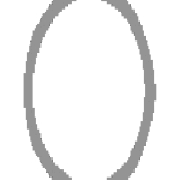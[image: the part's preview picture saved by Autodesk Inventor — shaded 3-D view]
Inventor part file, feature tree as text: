
AUTODESK INVENTOR PART (.ipt)
format: ipt  version: 2021 (Build 250183000, 183)  size: 112,640 bytes
history: native  units: in
note: dims shown in document units (in); Inventor stores cm internally (conversion verified against a paired STEP export)
features: other x4, sketch x3, plane x1
ambient origin geometry x8: Origin, YZ Plane, XZ Plane, XY Plane, X Axis, Y Axis, Z Axis, Center Point
bodies: Solid1 (feature_tree), Body (feature_tree)
feature tree (8):
  other  "Driven Length"
  other  "Frame Generator"
  other  "Start Plane"
  other  "End Plane"
  sketch  "Sketch"  dims[d2=29.4in d4=-0.0in d5=29.4in d6=0.12in d7=0.0in d8=90.0deg d9=29.4in]
  sketch  "Sketch2"  dims[d0=1.0in]
  plane  "Work Plane3"
  sketch  "Sketch3"  dims[d1=0.065in]
